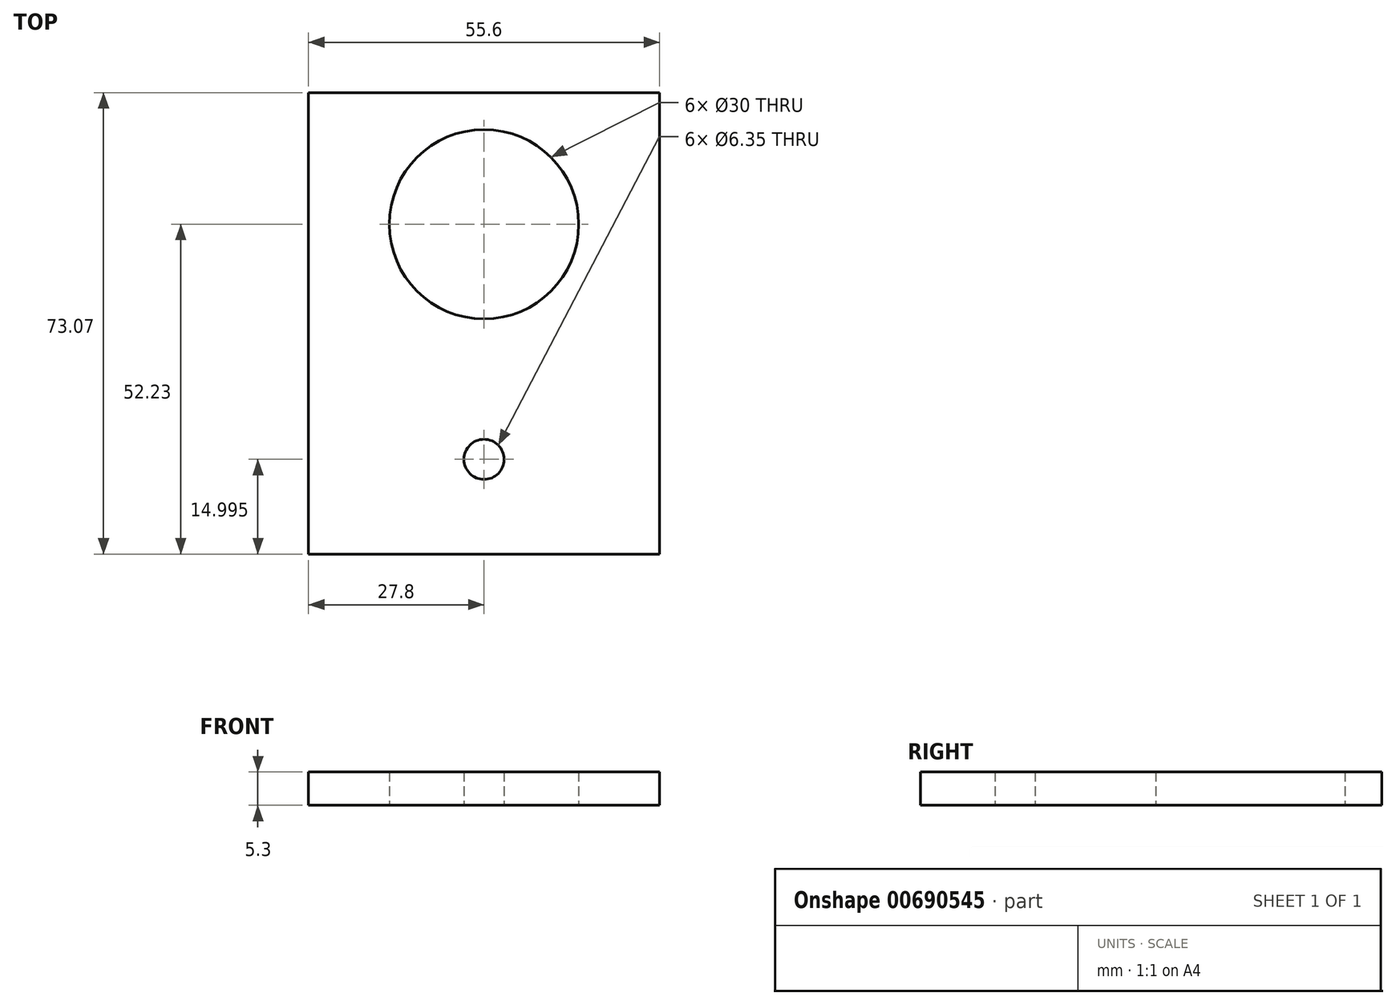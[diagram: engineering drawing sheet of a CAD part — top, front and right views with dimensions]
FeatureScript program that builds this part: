
annotation { "Feature Type Name" : "Feature", "Feature Type Description" : "" }
export const myFeature = defineFeature(function(context is Context, id is Id, definition is map)
    precondition{}
    {
        {
            var Q0;
            Q0=qCreatedBy(makeId("Top.planeOp"),FACE);
            var sketch = newSketch(context, id + "F0", { "sketchPlane" : qUnion([Q0])});
            skLineSegment(sketch, "E0.bottom", {"start": v(27.8, 21.54) * mm, "end": v(-27.8, 21.54) * mm});
            skLineSegment(sketch, "E0.top", {"start": v(27.8, -21.54) * mm, "end": v(-27.8, -21.54) * mm});
            skLineSegment(sketch, "E0.left", {"start": v(27.8, 21.54) * mm, "end": v(27.8, -21.54) * mm});
            skLineSegment(sketch, "E0.right", {"start": v(-27.8, 21.54) * mm, "end": v(-27.8, -21.54) * mm});
            skPoint(sketch, "E0.middle", {"position": v(0, 0) * mm});
            skCircle(sketch, "E1", {"center": v(0, 0.7) * mm, "radius": 15 * mm});
            skLineSegment(sketch, "E2", {"start": v(-27.8, -21.54) * mm, "end": v(-27.8, -51.53) * mm});
            skLineSegment(sketch, "E3", {"start": v(-27.8, -51.53) * mm, "end": v(27.8, -51.53) * mm});
            skLineSegment(sketch, "E4", {"start": v(27.8, -51.53) * mm, "end": v(27.8, -21.54) * mm});
            skCircle(sketch, "E5", {"center": v(0, -36.53) * mm, "radius": 3.18 * mm});
            skSolve(sketch);
        }
        {
            var Q0;
            Q0 = qSketchRegion(id + "F0", true);
            extrude(context, id + "F1", {"entities" : qUnion([Q0]), "depth" : 5.3 * mm, "offsetDistance" : 25 * mm});
        }
    });
